# Revit family: SIGUR E510
name_source: partatom
category: Датчики
revit_build: Autodesk Revit 2018 (Build: 20180423_1000(x64)
units: mm (PartAtom-declared; Revit-internal decimal feet)

## family parameters
Общий = Нет
Основа = Грань
При загрузке вырезать с полостями = Нет
Размер круглого соединителя = Использовать диаметр
Сохранять ориентацию аннотаций = Нет
Тип детали = Нормальный
Точка расчета площади = Да

## types (1)
- SIGUR E510
    ADSK_URL страницы изделия = https://www.sigur.com
    ADSK_Версия Revit = Revit 2018
    ADSK_Версия семейства = v1
    ADSK_Единица измерения = шт.
    ADSK_Завод-изготовитель = ООО Промавтоматика-КД, Нижний Новгород
    ADSK_Классификация нагрузок = Прочее
    ADSK_Количество = 1
    ADSK_Количество фаз = 1
    ADSK_Количество фаз числовое = 1
    ADSK_Коэффициент мощности = 0.9
    ADSK_Марка = SIGUR
    ADSK_Масса = 1.542
    ADSK_Масса_Текст = 1.542
    ADSK_Материал = SIGUR_Белый
    ADSK_Наименование = Контроллер E510
    ADSK_Наименование краткое = E510
    ADSK_Напряжение = 15 В
    ADSK_Номинальная мощность = 4 Вт
    ADSK_Обозначение = SIGUR
    ADSK_Полная мощность = 4 В·А
    ADSK_Размер_Высота = 240 мм
    ADSK_Размер_Толщина = 57 мм
    ADSK_Размер_Ширина = 260 мм
    ADSK_Ток = 0 А
    URL = https://www.sigur.com
    Изготовитель = SIGUR
    Изготовитель (телефон) = 8 (800) 700-31-83
    Отметка по умолчанию = 0 мм
    Разработчик = ООО ПРОРУБИМ
    Разработчик (URL) = http://prorubim.com
    Разработчик (телефон) = +7(495)649-85-43
    УГО_Размер = 240 мм
